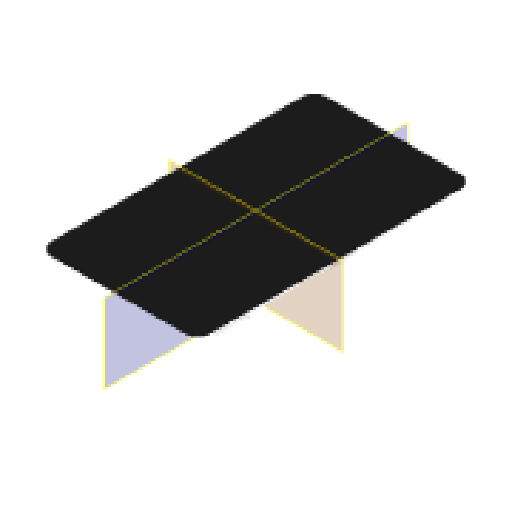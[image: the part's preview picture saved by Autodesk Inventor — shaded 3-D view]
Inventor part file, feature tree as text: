
AUTODESK INVENTOR PART (.ipt)
format: ipt  version: 2024.1 (Build 281209000, 209)  size: 7,621,120 bytes
history: native  units: mm
features: other x246, plane x2
ambient origin geometry x8: Origin, YZ Plane, XZ Plane, XY Plane, X Axis, Y Axis, Z Axis, Center Point
bodies: Volumenkörper1 (feature_tree), Volumenkörper2 (feature_tree), Volumenkörper3 (feature_tree), Volumenkörper4 (feature_tree), Volumenkörper5 (feature_tree), Volumenkörper6 (feature_tree), Volumenkörper7 (feature_tree), Volumenkörper8 (feature_tree), Volumenkörper9 (feature_tree), Volumenkörper10 (feature_tree), Volumenkörper11 (feature_tree), Volumenkörper12 (feature_tree), Volumenkörper13 (feature_tree), Volumenkörper14 (feature_tree), Volumenkörper15 (feature_tree), Volumenkörper16 (feature_tree), Volumenkörper17 (feature_tree), Volumenkörper18 (feature_tree), Volumenkörper19 (feature_tree), Volumenkörper20 (feature_tree), Volumenkörper21 (feature_tree), Volumenkörper22 (feature_tree), Volumenkörper23 (feature_tree), Volumenkörper24 (feature_tree), Volumenkörper25 (feature_tree), Volumenkörper26 (feature_tree), Volumenkörper27 (feature_tree), Volumenkörper28 (feature_tree), Volumenkörper29 (feature_tree), Volumenkörper30 (feature_tree), Volumenkörper31 (feature_tree), Volumenkörper32 (feature_tree), Volumenkörper33 (feature_tree), Volumenkörper34 (feature_tree), Volumenkörper35 (feature_tree), Volumenkörper36 (feature_tree), Volumenkörper37 (feature_tree), Volumenkörper38 (feature_tree), Volumenkörper39 (feature_tree), Volumenkörper40 (feature_tree), Volumenkörper41 (feature_tree), Volumenkörper42 (feature_tree), Volumenkörper43 (feature_tree), Volumenkörper44 (feature_tree), Volumenkörper45 (feature_tree), Volumenkörper46 (feature_tree), Volumenkörper47 (feature_tree), Volumenkörper48 (feature_tree), Volumenkörper49 (feature_tree), Volumenkörper50 (feature_tree), Volumenkörper51 (feature_tree), Volumenkörper52 (feature_tree), Volumenkörper53 (feature_tree), Volumenkörper54 (feature_tree), Volumenkörper55 (feature_tree), Volumenkörper56 (feature_tree), Volumenkörper57 (feature_tree), Volumenkörper58 (feature_tree), Volumenkörper59 (feature_tree), Volumenkörper60 (feature_tree), Volumenkörper61 (feature_tree), Volumenkörper62 (feature_tree), Volumenkörper63 (feature_tree), Volumenkörper64 (feature_tree), Volumenkörper65 (feature_tree), Volumenkörper66 (feature_tree), Volumenkörper67 (feature_tree), Volumenkörper68 (feature_tree), Volumenkörper69 (feature_tree), Volumenkörper70 (feature_tree), Volumenkörper71 (feature_tree), Volumenkörper72 (feature_tree), Volumenkörper73 (feature_tree), Volumenkörper74 (feature_tree), Volumenkörper75 (feature_tree), Volumenkörper76 (feature_tree), Volumenkörper77 (feature_tree), Volumenkörper78 (feature_tree), Volumenkörper79 (feature_tree), Volumenkörper80 (feature_tree), Volumenkörper81 (feature_tree), Volumenkörper82 (feature_tree), Volumenkörper83 (feature_tree), Volumenkörper84 (feature_tree), Volumenkörper85 (feature_tree), Volumenkörper86 (feature_tree), Volumenkörper87 (feature_tree), Volumenkörper88 (feature_tree), Volumenkörper89 (feature_tree), Volumenkörper90 (feature_tree), Volumenkörper91 (feature_tree), Volumenkörper92 (feature_tree), Volumenkörper93 (feature_tree), Volumenkörper94 (feature_tree), Volumenkörper95 (feature_tree), Volumenkörper96 (feature_tree), Volumenkörper97 (feature_tree), Volumenkörper98 (feature_tree), Volumenkörper99 (feature_tree), Volumenkörper100 (feature_tree), Volumenkörper101 (feature_tree), Volumenkörper102 (feature_tree), Volumenkörper103 (feature_tree), Volumenkörper104 (feature_tree), Volumenkörper105 (feature_tree), Volumenkörper106 (feature_tree), Volumenkörper107 (feature_tree), Volumenkörper108 (feature_tree), Volumenkörper109 (feature_tree), Volumenkörper110 (feature_tree), Volumenkörper111 (feature_tree), Volumenkörper112 (feature_tree), Volumenkörper113 (feature_tree), Volumenkörper114 (feature_tree), Volumenkörper115 (feature_tree), Volumenkörper116 (feature_tree), Volumenkörper117 (feature_tree), Volumenkörper118 (feature_tree), Volumenkörper119 (feature_tree), Volumenkörper120 (feature_tree), Volumenkörper121 (feature_tree), Volumenkörper122 (feature_tree), Volumenkörper123 (feature_tree), Volumenkörper124 (feature_tree), Volumenkörper125 (feature_tree), Volumenkörper126 (feature_tree), Volumenkörper127 (feature_tree), Volumenkörper128 (feature_tree), Volumenkörper129 (feature_tree), Volumenkörper130 (feature_tree), Volumenkörper131 (feature_tree), Volumenkörper132 (feature_tree), Volumenkörper133 (feature_tree), Volumenkörper134 (feature_tree), Volumenkörper135 (feature_tree), Volumenkörper136 (feature_tree), Volumenkörper137 (feature_tree), Volumenkörper138 (feature_tree), Volumenkörper139 (feature_tree), Volumenkörper140 (feature_tree), Volumenkörper141 (feature_tree), Volumenkörper142 (feature_tree), Volumenkörper143 (feature_tree), Volumenkörper144 (feature_tree), Volumenkörper145 (feature_tree), Volumenkörper146 (feature_tree), Volumenkörper147 (feature_tree), Volumenkörper148 (feature_tree), Volumenkörper149 (feature_tree), Volumenkörper150 (feature_tree), Volumenkörper151 (feature_tree), Volumenkörper152 (feature_tree), Volumenkörper153 (feature_tree), Volumenkörper154 (feature_tree), Volumenkörper155 (feature_tree), Volumenkörper156 (feature_tree), Volumenkörper157 (feature_tree), Volumenkörper158 (feature_tree), Volumenkörper159 (feature_tree), Volumenkörper160 (feature_tree), Volumenkörper161 (feature_tree), Volumenkörper162 (feature_tree), Volumenkörper163 (feature_tree), Volumenkörper164 (feature_tree), Volumenkörper165 (feature_tree), Volumenkörper166 (feature_tree), Volumenkörper167 (feature_tree), Volumenkörper168 (feature_tree), Volumenkörper169 (feature_tree), Volumenkörper170 (feature_tree), Volumenkörper171 (feature_tree), Volumenkörper172 (feature_tree), Volumenkörper173 (feature_tree), Volumenkörper174 (feature_tree), Volumenkörper175 (feature_tree), Volumenkörper176 (feature_tree), Volumenkörper177 (feature_tree), Volumenkörper178 (feature_tree), Volumenkörper179 (feature_tree), Volumenkörper180 (feature_tree), Volumenkörper181 (feature_tree), Volumenkörper182 (feature_tree), Volumenkörper183 (feature_tree), Volumenkörper184 (feature_tree), Volumenkörper185 (feature_tree), Volumenkörper186 (feature_tree), Volumenkörper187 (feature_tree), Volumenkörper188 (feature_tree), Volumenkörper189 (feature_tree), Volumenkörper190 (feature_tree), Volumenkörper191 (feature_tree), Volumenkörper192 (feature_tree), Volumenkörper193 (feature_tree), Volumenkörper194 (feature_tree), Volumenkörper195 (feature_tree), Volumenkörper196 (feature_tree), Volumenkörper197 (feature_tree), Volumenkörper198 (feature_tree), Volumenkörper199 (feature_tree), Volumenkörper200 (feature_tree), Volumenkörper201 (feature_tree), Volumenkörper202 (feature_tree), Volumenkörper203 (feature_tree), Volumenkörper204 (feature_tree), Volumenkörper205 (feature_tree), Volumenkörper206 (feature_tree), Volumenkörper207 (feature_tree), Volumenkörper208 (feature_tree), Volumenkörper209 (feature_tree), Volumenkörper210 (feature_tree), Volumenkörper211 (feature_tree), Volumenkörper212 (feature_tree), Volumenkörper213 (feature_tree), Volumenkörper214 (feature_tree), Volumenkörper215 (feature_tree), Volumenkörper216 (feature_tree), Volumenkörper217 (feature_tree), Volumenkörper218 (feature_tree), Volumenkörper219 (feature_tree), Volumenkörper220 (feature_tree), Volumenkörper221 (feature_tree), Volumenkörper222 (feature_tree), Volumenkörper223 (feature_tree), Volumenkörper224 (feature_tree), Volumenkörper225 (feature_tree), Volumenkörper226 (feature_tree), Volumenkörper227 (feature_tree), Volumenkörper228 (feature_tree), Volumenkörper229 (feature_tree), Volumenkörper230 (feature_tree), Volumenkörper231 (feature_tree), Volumenkörper232 (feature_tree), Volumenkörper233 (feature_tree), Volumenkörper234 (feature_tree), Volumenkörper235 (feature_tree), Volumenkörper236 (feature_tree), Volumenkörper237 (feature_tree), Volumenkörper238 (feature_tree), Volumenkörper239 (feature_tree), Volumenkörper240 (feature_tree), Volumenkörper241 (feature_tree), Volumenkörper242 (feature_tree), Volumenkörper243 (feature_tree), Volumenkörper244 (feature_tree), Volumenkörper245 (feature_tree), Volumenkörper246 (feature_tree)
feature tree (248):
  plane  "Arbeitsebene1"
  plane  "Arbeitsebene2"
  other  "raspberry pi display_1:1"
  other  "raspberry pi display_1:2"
  other  "raspberry pi display_1:3"
  other  "Raspberry Pi 3 _1:1"
  other  "Raspberry Pi 3 _1:2"
  other  "Raspberry Pi 3 _1:3"
  other  "Raspberry Pi 3 _1:4"
  other  "Raspberry Pi 3 _1:5"
  other  "Raspberry Pi 3 _1:6"
  other  "Raspberry Pi 3 _1:7"
  other  "Raspberry Pi 3 _1:8"
  other  "Raspberry Pi 3 _1:9"
  other  "Raspberry Pi 3 _1:10"
  other  "Raspberry Pi 3 _1:11"
  other  "Raspberry Pi 3 _1:12"
  other  "Raspberry Pi 3 _1:13"
  other  "Raspberry Pi 3 _1:14"
  other  "Raspberry Pi 3 _1:15"
  other  "Raspberry Pi 3 _1:16"
  other  "Raspberry Pi 3 _1:17"
  other  "Raspberry Pi 3 _1:18"
  other  "Raspberry Pi 3 _1:19"
  other  "Raspberry Pi 3 _1:20"
  other  "Raspberry Pi 3 _1:21"
  other  "Raspberry Pi 3 _1:22"
  other  "Raspberry Pi 3 _1:23"
  other  "Raspberry Pi 3 _1:24"
  other  "Raspberry Pi 3 _1:25"
  other  "Raspberry Pi 3 _1:26"
  other  "Raspberry Pi 3 _1:27"
  other  "Raspberry Pi 3 _1:28"
  other  "Raspberry Pi 3 _1:29"
  other  "Raspberry Pi 3 _1:30"
  other  "Raspberry Pi 3 _1:31"
  other  "Raspberry Pi 3 _1:32"
  other  "Raspberry Pi 3 _1:33"
  other  "Raspberry Pi 3 _1:34"
  other  "Raspberry Pi 3 _1:35"
  other  "Raspberry Pi 3 _1:36"
  other  "Raspberry Pi 3 _1:37"
  other  "Raspberry Pi 3 _1:38"
  other  "Raspberry Pi 3 _1:39"
  other  "Raspberry Pi 3 _1:40"
  other  "Raspberry Pi 3 _1:41"
  other  "Raspberry Pi 3 _1:42"
  other  "Raspberry Pi 3 _1:43"
  other  "Raspberry Pi 3 _1:44"
  other  "Raspberry Pi 3 _1:45"
  other  "Raspberry Pi 3 _1:46"
  other  "Raspberry Pi 3 _1:47"
  other  "Raspberry Pi 3 _1:48"
  other  "Raspberry Pi 3 _1:49"
  other  "Raspberry Pi 3 _1:50"
  other  "Raspberry Pi 3 _1:51"
  other  "Raspberry Pi 3 _1:52"
  other  "Raspberry Pi 3 _1:53"
  other  "Raspberry Pi 3 _1:54"
  other  "Raspberry Pi 3 _1:55"
  other  "Raspberry Pi 3 _1:56"
  other  "Raspberry Pi 3 _1:57"
  other  "Raspberry Pi 3 _1:58"
  other  "Raspberry Pi 3 _1:59"
  other  "Raspberry Pi 3 _1:60"
  other  "Raspberry Pi 3 _1:61"
  other  "Raspberry Pi 3 _1:62"
  other  "Raspberry Pi 3 _1:63"
  other  "Raspberry Pi 3 _1:64"
  other  "Raspberry Pi 3 _1:65"
  other  "Raspberry Pi 3 _1:66"
  other  "Raspberry Pi 3 _1:67"
  other  "Raspberry Pi 3 _1:68"
  other  "Raspberry Pi 3 _1:69"
  other  "Raspberry Pi 3 _1:70"
  other  "Raspberry Pi 3 _1:71"
  other  "Raspberry Pi 3 _1:72"
  other  "Raspberry Pi 3 _1:73"
  other  "Raspberry Pi 3 _1:74"
  other  "Raspberry Pi 3 _1:75"
  other  "Raspberry Pi 3 _1:76"
  other  "Raspberry Pi 3 _1:77"
  other  "Raspberry Pi 3 _1:78"
  other  "Raspberry Pi 3 _1:79"
  other  "Raspberry Pi 3 _1:80"
  other  "Raspberry Pi 3 _1:81"
  other  "Raspberry Pi 3 _1:82"
  other  "Raspberry Pi 3 _1:83"
  other  "Raspberry Pi 3 _1:84"
  other  "Raspberry Pi 3 _1:85"
  other  "Raspberry Pi 3 _1:86"
  other  "Raspberry Pi 3 _1:87"
  other  "Raspberry Pi 3 _1:88"
  other  "Raspberry Pi 3 _1:89"
  other  "Raspberry Pi 3 _1:90"
  other  "Raspberry Pi 3 _1:91"
  other  "Raspberry Pi 3 _1:92"
  other  "Raspberry Pi 3 _1:93"
  other  "Raspberry Pi 3 _1:94"
  other  "Raspberry Pi 3 _1:95"
  other  "Raspberry Pi 3 _1:96"
  other  "Raspberry Pi 3 _1:97"
  other  "Raspberry Pi 3 _1:98"
  other  "Raspberry Pi 3 _1:99"
  other  "Raspberry Pi 3 _1:100"
  other  "Raspberry Pi 3 _1:101"
  other  "Raspberry Pi 3 _1:102"
  other  "Raspberry Pi 3 _1:103"
  other  "Raspberry Pi 3 _1:104"
  other  "Raspberry Pi 3 _1:105"
  other  "Raspberry Pi 3 _1:106"
  other  "Raspberry Pi 3 _1:107"
  other  "Raspberry Pi 3 _1:108"
  other  "Raspberry Pi 3 _1:109"
  other  "Raspberry Pi 3 _1:110"
  other  "Raspberry Pi 3 _1:111"
  other  "Raspberry Pi 3 _1:112"
  other  "Raspberry Pi 3 _1:113"
  other  "Raspberry Pi 3 _1:114"
  other  "Raspberry Pi 3 _1:115"
  other  "Raspberry Pi 3 _1:116"
  other  "Raspberry Pi 3 _1:117"
  other  "Raspberry Pi 3 _1:118"
  other  "Raspberry Pi 3 _1:119"
  other  "Raspberry Pi 3 _1:120"
  other  "Raspberry Pi 3 _1:121"
  other  "Raspberry Pi 3 _1:122"
  other  "Raspberry Pi 3 _1:123"
  other  "Raspberry Pi 3 _1:124"
  other  "Raspberry Pi 3 _1:125"
  other  "Raspberry Pi 3 _1:126"
  other  "Raspberry Pi 3 _1:127"
  other  "Raspberry Pi 3 _1:128"
  other  "Raspberry Pi 3 _1:129"
  other  "Raspberry Pi 3 _1:130"
  other  "Raspberry Pi 3 _1:131"
  other  "Raspberry Pi 3 _1:132"
  other  "Raspberry Pi 3 _1:133"
  other  "Raspberry Pi 3 _1:134"
  other  "Raspberry Pi 3 _1:135"
  other  "Raspberry Pi 3 _1:136"
  other  "Raspberry Pi 3 _1:137"
  other  "Raspberry Pi 3 _1:138"
  other  "Raspberry Pi 3 _1:139"
  other  "Raspberry Pi 3 _1:140"
  other  "Raspberry Pi 3 _1:141"
  other  "Raspberry Pi 3 _1:142"
  other  "Raspberry Pi 3 _1:143"
  other  "Raspberry Pi 3 _1:144"
  other  "Raspberry Pi 3 _1:145"
  other  "Raspberry Pi 3 _1:146"
  other  "Raspberry Pi 3 _1:147"
  other  "Raspberry Pi 3 _1:148"
  other  "Raspberry Pi 3 _1:149"
  other  "Raspberry Pi 3 _1:150"
  other  "Raspberry Pi 3 _1:151"
  other  "Raspberry Pi 3 _1:152"
  other  "Raspberry Pi 3 _1:153"
  other  "Raspberry Pi 3 _1:154"
  other  "Raspberry Pi 3 _1:155"
  other  "Raspberry Pi 3 _1:156"
  other  "Raspberry Pi 3 _1:157"
  other  "Raspberry Pi 3 _1:158"
  other  "Raspberry Pi 3 _1:159"
  other  "Raspberry Pi 3 _1:160"
  other  "Raspberry Pi 3 _1:161"
  other  "Raspberry Pi 3 _1:162"
  other  "Raspberry Pi 3 _1:163"
  other  "Raspberry Pi 3 _1:164"
  other  "Raspberry Pi 3 _1:165"
  other  "Raspberry Pi 3 _1:166"
  other  "Raspberry Pi 3 _1:167"
  other  "Raspberry Pi 3 _1:168"
  other  "Raspberry Pi 3 _1:169"
  other  "Raspberry Pi 3 _1:170"
  other  "Raspberry Pi 3 _1:171"
  other  "Raspberry Pi 3 _1:172"
  other  "Raspberry Pi 3 _1:173"
  other  "Raspberry Pi 3 _1:174"
  other  "Raspberry Pi 3 _1:175"
  other  "Raspberry Pi 3 _1:176"
  other  "Raspberry Pi 3 _1:177"
  other  "Raspberry Pi 3 _1:178"
  other  "Raspberry Pi 3 _1:179"
  other  "Raspberry Pi 3 _1:180"
  other  "Raspberry Pi 3 _1:181"
  other  "Raspberry Pi 3 _1:182"
  other  "Raspberry Pi 3 _1:183"
  other  "Raspberry Pi 3 _1:184"
  other  "Raspberry Pi 3 _1:185"
  other  "Raspberry Pi 3 _1:186"
  other  "Raspberry Pi 3 _1:187"
  other  "Raspberry Pi 3 _1:188"
  other  "Raspberry Pi 3 _1:189"
  other  "Raspberry Pi 3 _1:190"
  other  "Raspberry Pi 3 _1:191"
  other  "Raspberry Pi 3 _1:192"
  other  "Raspberry Pi 3 _1:193"
  other  "Raspberry Pi 3 _1:194"
  other  "Raspberry Pi 3 _1:195"
  other  "Raspberry Pi 3 _1:196"
  other  "Raspberry Pi 3 _1:197"
  other  "Raspberry Pi 3 _1:198"
  other  "Raspberry Pi 3 _1:199"
  other  "Raspberry Pi 3 _1:200"
  other  "Raspberry Pi 3 _1:201"
  other  "Raspberry Pi 3 _1:202"
  other  "Raspberry Pi 3 _1:203"
  other  "Raspberry Pi 3 _1:204"
  other  "Raspberry Pi 3 _1:205"
  other  "Raspberry Pi 3 _1:206"
  other  "Raspberry Pi 3 _1:207"
  other  "Raspberry Pi 3 _1:208"
  other  "Raspberry Pi 3 _1:209"
  other  "Raspberry Pi 3 _1:210"
  other  "Raspberry Pi 3 _1:211"
  other  "Raspberry Pi 3 _1:212"
  other  "Raspberry Pi 3 _1:213"
  other  "Raspberry Pi 3 _1:214"
  other  "Raspberry Pi 3 _1:215"
  other  "Raspberry Pi 3 _1:216"
  other  "Raspberry Pi 3 _1:217"
  other  "raspberry pi display module_1:1"
  other  "raspberry pi display module_1:2"
  other  "raspberry pi display module_1:3"
  other  "raspberry pi display module_1:4"
  other  "raspberry pi display module_1:5"
  other  "raspberry pi display module_1:6"
  other  "raspberry pi display module_1:7"
  other  "raspberry pi display module_1:8"
  other  "raspberry pi display module_1:9"
  other  "raspberry pi display module_1:10"
  other  "raspberry pi display module_1:11"
  other  "raspberry pi display module_1:12"
  other  "raspberry pi display module_1:13"
  other  "raspberry pi display module_1:14"
  other  "стойка 12мм_1:1"
  other  "стойка 12мм_2:1"
  other  "стойка 12мм_3:1"
  other  "стойка 12мм_4:1"
  other  "cables_1:1"
  other  "cables_1:2"
  other  "cables_1:3"
  other  "cables_1:4"
  other  "ISO 7045 H M2,5 x 3 - 4.8 - H_1:1"
  other  "ISO 7045 H M2,5 x 3 - 4.8 - H_2:1"
  other  "ISO 7045 H M2,5 x 3 - 4.8 - H_3:1"
  other  "ISO 7045 H M2,5 x 3 - 4.8 - H_4:1"
